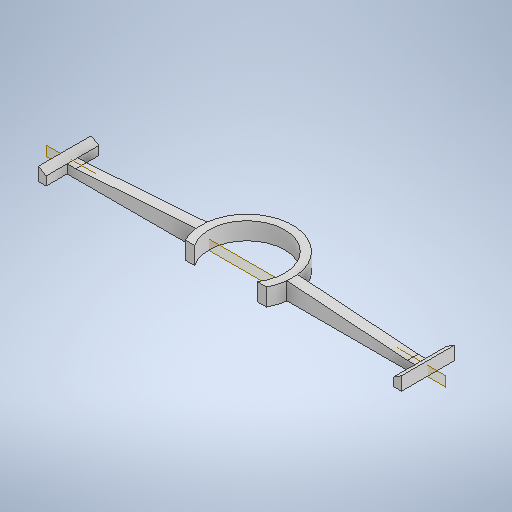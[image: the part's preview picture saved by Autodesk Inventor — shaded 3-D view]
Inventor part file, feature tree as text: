
AUTODESK INVENTOR PART (.ipt)
format: ipt  version: 2025.1 (Build 291241000, 241)  size: 343,040 bytes
history: native  units: mm
features: extrude x6, sketch x6, plane x1
ambient origin geometry x8: Origin, YZ Plane, XZ Plane, XY Plane, X Axis, Y Axis, Z Axis, Center Point
bodies: Volumenkörper1 (feature_tree)
feature tree (13):
  extrude  "Extrusion1"  Depth=2.85mm
  plane  "Arbeitsebene1"
  extrude  "Extrusion2"  Depth=2.85mm
  extrude  "Extrusion3"  Depth=19.7mm
  extrude  "Extrusion4"  Depth=6.5mm TaperAngle=0.0deg
  extrude  "Extrusion7"  Depth=45.0mm
  extrude  "Extrusion8"  Depth=3.25mm TaperAngle=0.0deg
  sketch  "Skizze1"  dims[d0=135.6mm d1=4.0mm d2=3.25mm d3=0.0mm d4=2.85mm]
  sketch  "Skizze2"  dims[d5=1.75mm d6=2.85mm]
  sketch  "Skizze3"  dims[d7=19.7mm d8=0.0mm d9=32.0mm]
  sketch  "Skizze4"  dims[d10=0.0mm d11=0.0mm d15=6.5mm d16=0.0mm]
  sketch  "Skizze7"  dims[d27=3.0mm d28=28.14mm d29=7.84mm d30=45.0mm]
  sketch  "Skizze8"  dims[d31=45.0mm d32=3.25mm d33=0.0mm d34=0.0mm d35=0.0mm d17=0.5mm d18=0.872665mm]
